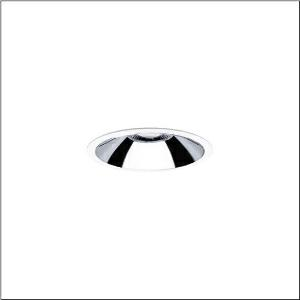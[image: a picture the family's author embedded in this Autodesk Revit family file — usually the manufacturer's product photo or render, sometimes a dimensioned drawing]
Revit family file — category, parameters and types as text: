
# Revit family: lunis_21_l_51db15md3c
name_source: partatom
category: Lighting Fixtures
units: mm (PartAtom-declared; Revit-internal decimal feet)

## family parameters
Cut with Voids When Loaded = No
Host = Face
Light Source = No
Part Type = Normal
Room Calculation Point = No
Round Connector Dimension = Use Diameter
Shared = No

## types (1)
- --- (1 x LED, 1670 lm, 13.8 W, 3000K)
    Apparent Load = 14 VA
    CIE Flux Codes = 90 99 100 100 100
    Color Rendering = 80
    Color Temperature = 3000K
    Default Elevation = 1800 mm
    Description = Lunis 21,  L, downlight, of PC, light emission: direct distribution, LED rated luminous flux: 1.670lm, light colour: 830, control gear: ECG, with terminal, 3-pole, mains connection: 220..240V, AC, housing, round, of diecast aluminium, traffic white (RAL 9016), diameter: 162mm, protection rating (complete): IP20, protection rating (on room side): IP54, insulation class (complete): insulation class II (safety insulation), certification: CE, impact resistance: IK02, packaging unit: 1 piece
    Height = 0 mm  [stored 0 ft]
    Lamp = 1 x LED
    Lamp Light Flux = 1670 lm
    Lamp Power = 13.8 W
    Lamp count = 1
    Length = 162 mm
    Luminous efficacy = 121 lm/W
    Manufacturer = Siteco
    ModVariant = No
    Model = 51DB15MD3C
    Mounting Place = Ceiling
    Mounting Type = Recessed
    Number of Poles = 1
    OnlyDefault = Yes
    Power Factor = 1
    Product Name = Lunis 21 L
    Product group = downlight
    ProductGroupID = 400
    Protection Class = Protection class II
    Protection Degree = IP 20
    RLX_Detail_Level = 1
    RLX_Emergency_Light_Flux = 0 lm
    RLX_Emergency_Type = 0
    RLX_Emergency_Type_DB = No
    RlxData = <blob elided: 21793 chars, md5=9b161af9>
    Socket = socket
    Standby Power = 0 W
    System Light Flux = 1670 lm
    System Power = 14 W
    Type Comments = factory setting: luminous flux: 100 % | (ON | ON)
    Type Image = l_1287387.jpg
    URL = http://relux.com
    VarID = @adj_099561
    Voltage = 0 V
    Weight = 0.00 kg
    Width = 0 mm  [stored 0 ft]

note: [stored X ft] marks values corroborated as IEEE doubles in the binary element streams (Revit-internal decimal feet)

## geometry (parser evidence)
native form markers: Blend x4, Sweep x9
no freeform markers — native parametric forms only
